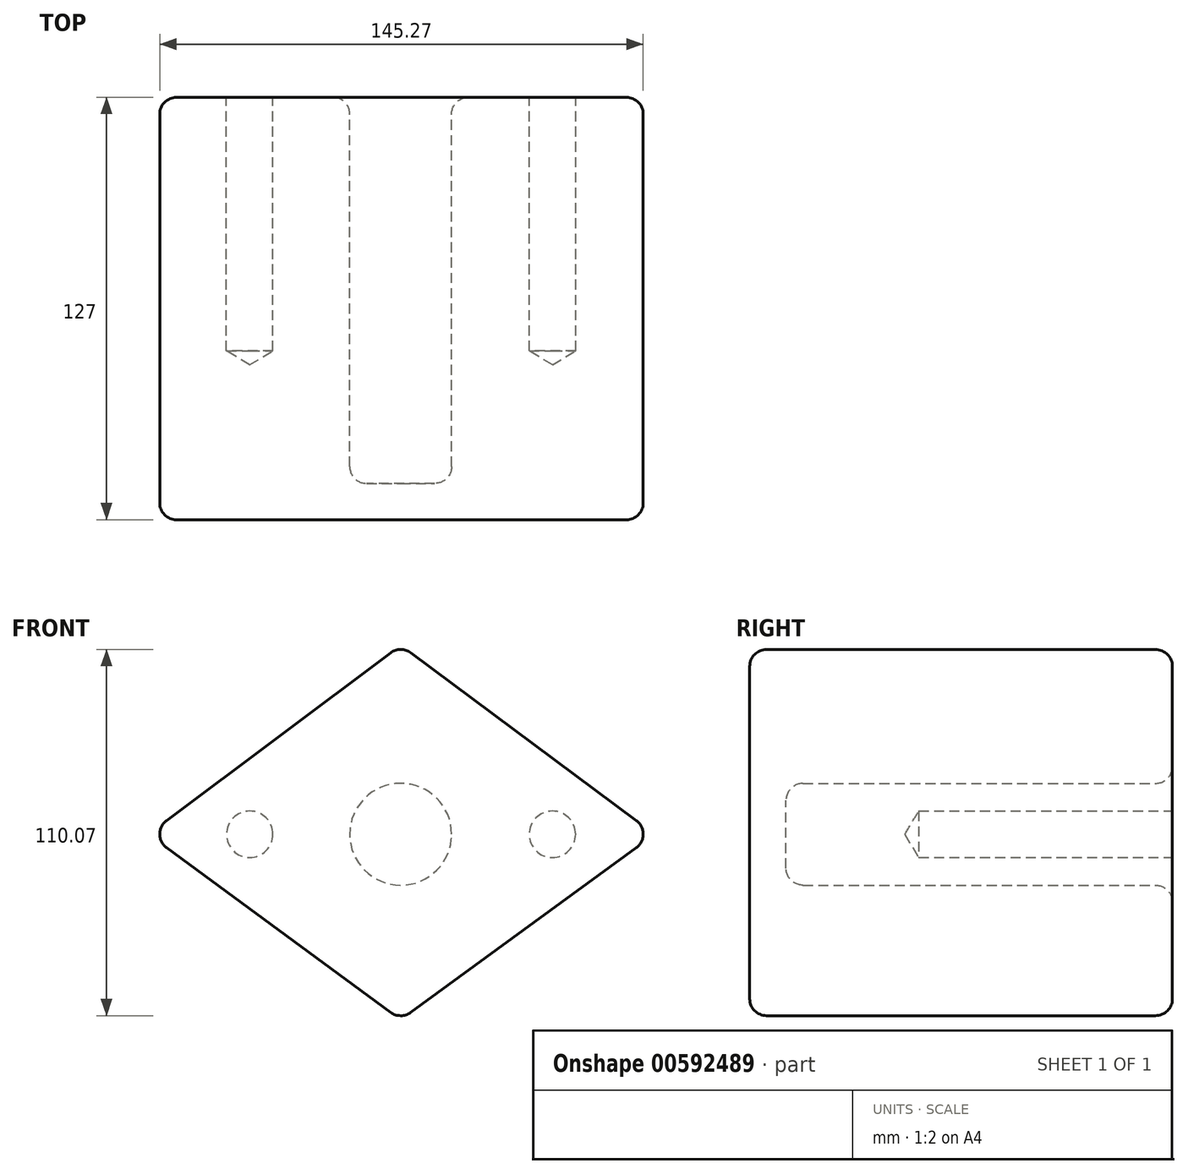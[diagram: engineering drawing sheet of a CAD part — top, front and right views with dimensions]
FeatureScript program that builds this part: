
annotation { "Feature Type Name" : "Feature", "Feature Type Description" : "" }
export const myFeature = defineFeature(function(context is Context, id is Id, definition is map)
    precondition{}
    {
        {
            var Q0;
            Q0=qCreatedBy(makeId("Front.planeOp"),FACE);
            var sketch = newSketch(context, id + "F0", { "sketchPlane" : qUnion([Q0])});
            skLineSegment(sketch, "E0", {"start": v(0, 0) * mm, "end": v(0, 56.8) * mm});
            skLineSegment(sketch, "E1", {"start": v(0, 56.8) * mm, "end": v(76.37, 0) * mm});
            skLineSegment(sketch, "E2", {"start": v(0, 0) * mm, "end": v(76.37, 0) * mm});
            skLineSegment(sketch, "E3", {"start": v(0, 0) * mm, "end": v(0, -55.74) * mm});
            skLineSegment(sketch, "E4", {"start": v(76.37, 0) * mm, "end": v(0, -55.74) * mm});
            skLineSegment(sketch, "E5", {"start": v(0, 0) * mm, "end": v(-75.83, 0) * mm});
            skLineSegment(sketch, "E6", {"start": v(0, -55.74) * mm, "end": v(-75.83, 0) * mm});
            skLineSegment(sketch, "E7", {"start": v(-75.83, 0) * mm, "end": v(0, 56.8) * mm});
            skCircle(sketch, "E8", {"center": v(0, 0) * mm, "radius": 7.17 * mm});
            skSolve(sketch);
        }
        {
            var Q0;
            {var subQ0=sQuery(id+"F0.wireOp",EDGE,"E7");Q0=makeQuery(id+"F0.imprint","IMPRINT",FACE,{"disambiguationData":[TD([[makeQuery(id+"F0.imprint","IMPRINT",EDGE,{"derivedFrom":subQ0}),-1.0]])]});}
            var Q1;
            {var subQ0=sQuery(id+"F0.wireOp",EDGE,"E1");Q1=makeQuery(id+"F0.imprint","IMPRINT",FACE,{"disambiguationData":[TD([[makeQuery(id+"F0.imprint","IMPRINT",EDGE,{"derivedFrom":subQ0}),-1.0]])]});}
            var Q2;
            {var subQ0=sQuery(id+"F0.wireOp",EDGE,"E4");Q2=makeQuery(id+"F0.imprint","IMPRINT",FACE,{"disambiguationData":[TD([[makeQuery(id+"F0.imprint","IMPRINT",EDGE,{"derivedFrom":subQ0}),-1.0]])]});}
            var Q3;
            {var subQ0=sQuery(id+"F0.wireOp",EDGE,"E6");Q3=makeQuery(id+"F0.imprint","IMPRINT",FACE,{"disambiguationData":[TD([[makeQuery(id+"F0.imprint","IMPRINT",EDGE,{"derivedFrom":subQ0}),-1.0]])]});}
            var Q4;
            {var subQ1=sQuery(id+"F0.wireOp",EDGE,"E2");var subQ3=sQuery(id+"F0.wireOp",EDGE,"E8");var subQ4=makeQuery(id+"F0.imprint","INTERSECT",VERTEX,{"derivedFrom":[subQ1,subQ3]});Q4=makeQuery(id+"F0.imprint","IMPRINT",FACE,{"disambiguationData":[TD([[makeQuery(id+"F0.imprint","IMPRINT",EDGE,{"disambiguationData":[TD([[subQ4,1.0]])],"derivedFrom":subQ3}),1.0]])]});}
            var Q5;
            {var subQ1=sQuery(id+"F0.wireOp",EDGE,"E0");var subQ3=sQuery(id+"F0.wireOp",EDGE,"E8");var subQ4=makeQuery(id+"F0.imprint","INTERSECT",VERTEX,{"derivedFrom":[subQ1,subQ3]});Q5=makeQuery(id+"F0.imprint","IMPRINT",FACE,{"disambiguationData":[TD([[makeQuery(id+"F0.imprint","IMPRINT",EDGE,{"disambiguationData":[TD([[subQ4,-1.0]])],"derivedFrom":subQ3}),1.0]])]});}
            var Q6;
            {var subQ1=sQuery(id+"F0.wireOp",EDGE,"E0");var subQ3=sQuery(id+"F0.wireOp",EDGE,"E8");var subQ4=makeQuery(id+"F0.imprint","INTERSECT",VERTEX,{"derivedFrom":[subQ1,subQ3]});Q6=makeQuery(id+"F0.imprint","IMPRINT",FACE,{"disambiguationData":[TD([[makeQuery(id+"F0.imprint","IMPRINT",EDGE,{"disambiguationData":[TD([[subQ4,1.0]])],"derivedFrom":subQ3}),1.0]])]});}
            var Q7;
            {var subQ1=sQuery(id+"F0.wireOp",EDGE,"E3");var subQ3=sQuery(id+"F0.wireOp",EDGE,"E8");var subQ4=makeQuery(id+"F0.imprint","INTERSECT",VERTEX,{"derivedFrom":[subQ1,subQ3]});Q7=makeQuery(id+"F0.imprint","IMPRINT",FACE,{"disambiguationData":[TD([[makeQuery(id+"F0.imprint","IMPRINT",EDGE,{"disambiguationData":[TD([[subQ4,1.0]])],"derivedFrom":subQ3}),1.0]])]});}
            extrude(context, id + "F1", {"entities" : qUnion([Q0, Q1, Q2, Q3, Q4, Q5, Q6, Q7]), "depth" : 25.4 * mm, "offsetDistance" : 25.4 * mm});
        }
        {
            var Q0;
            Q0=qCreatedBy(makeId("Front.planeOp"),FACE);
            var sketch = newSketch(context, id + "F2", { "sketchPlane" : qUnion([Q0])});
            skPoint(sketch, "E9", {"position": v(0, 0) * mm});
            skCircle(sketch, "E10", {"center": v(0, 0) * mm, "radius": 15.3 * mm});
            skSolve(sketch);
        }
        {
            var Q0;
            Q0=makeQuery(id+"F2.imprint","IMPRINT",FACE,{"disambiguationData":[TD([[makeQuery(id+"F2.imprint","IMPRINT",EDGE,{"derivedFrom":sQuery(id+"F2.wireOp",EDGE,"E10")}),1.0]])]});
            extrude(context, id + "F3", {"entities" : qUnion([Q0]), "operationType" : NewBodyOperationType.REMOVE, "depth" : 14.48 * mm, "offsetDistance" : 25.4 * mm});
        }
        {
            var Q0;
            Q0=makeQuery(id+"F1.opExtrude","CAP_FACE",FACE,{"disambiguationData":[OSD([sQuery(id+"F0.wireOp",EDGE,"E1"),sQuery(id+"F0.wireOp",EDGE,"E4"),sQuery(id+"F0.wireOp",EDGE,"E6"),sQuery(id+"F0.wireOp",EDGE,"E7")])],"isStart":true});
            extrude(context, id + "F4", {"entities" : qUnion([Q0]), "operationType" : NewBodyOperationType.ADD, "depth" : 101.6 * mm, "offsetDistance" : 25.4 * mm});
        }
        {
            var Q0;
            Q0=makeQuery(id+"F4.opExtrude","CAP_FACE",FACE,{"disambiguationData":[OSD([sQuery(id+"F0.wireOp",EDGE,"E1"),sQuery(id+"F0.wireOp",EDGE,"E4"),sQuery(id+"F0.wireOp",EDGE,"E6"),sQuery(id+"F0.wireOp",EDGE,"E7")])],"isStart":false});
            var sketch = newSketch(context, id + "F5", { "sketchPlane" : qUnion([Q0])});
            skCircle(sketch, "E11", {"center": v(-45.6, 0) * mm, "radius": 9.34 * mm});
            skCircle(sketch, "E12", {"center": v(47.08, 0) * mm, "radius": 9.04 * mm});
            skSolve(sketch);
        }
        {
            var Q0;
            Q0=sQuery(id+"F5.wireOp",VERTEX,"E11.center");
            var Q1;
            Q1=makeQuery(id+"F1.opExtrude","SWEPT_BODY",BODY,{"disambiguationData":[OSD([sQuery(id+"F0.wireOp",EDGE,"E1"),sQuery(id+"F0.wireOp",EDGE,"E4"),sQuery(id+"F0.wireOp",EDGE,"E6"),sQuery(id+"F0.wireOp",EDGE,"E7")])]});
            hole(context, id + "F6", {"style" : HoleStyle.C_BORE, "endStyle" : HoleEndStyle.BLIND, "holeDiameter" : 13.97 * mm, "cBoreDiameter" : 13.97 * mm, "cBoreDepth" : 6.35 * mm, "majorDiameter" : 6.35 * mm, "holeDepth" : 76.2 * mm, "isTappedThrough" : true, "tappedDepth" : 12.7 * mm, "tapClearance" : 3, "locations" : qUnion([Q0]), "scope" : qUnion([Q1])});
        }
        {
            var Q0;
            Q0=makeQuery(id+"F4.opExtrude","CAP_FACE",FACE,{"disambiguationData":[OSD([sQuery(id+"F0.wireOp",EDGE,"E1"),sQuery(id+"F0.wireOp",EDGE,"E4"),sQuery(id+"F0.wireOp",EDGE,"E6"),sQuery(id+"F0.wireOp",EDGE,"E7")])],"isStart":false});
            var sketch = newSketch(context, id + "F7", { "sketchPlane" : qUnion([Q0])});
            skCircle(sketch, "E13", {"center": v(45.35, 0) * mm, "radius": 9.24 * mm});
            skSolve(sketch);
        }
        {
            var Q0;
            Q0=sQuery(id+"F7.wireOp",VERTEX,"E13.center");
            var Q1;
            Q1=makeQuery(id+"F1.opExtrude","SWEPT_BODY",BODY,{"disambiguationData":[OSD([sQuery(id+"F0.wireOp",EDGE,"E1"),sQuery(id+"F0.wireOp",EDGE,"E4"),sQuery(id+"F0.wireOp",EDGE,"E6"),sQuery(id+"F0.wireOp",EDGE,"E7")])]});
            hole(context, id + "F8", {"style" : HoleStyle.C_BORE, "endStyle" : HoleEndStyle.BLIND, "holeDiameter" : 13.97 * mm, "cBoreDiameter" : 13.97 * mm, "cBoreDepth" : 6.35 * mm, "majorDiameter" : 6.35 * mm, "holeDepth" : 76.2 * mm, "isTappedThrough" : true, "tappedDepth" : 12.7 * mm, "tapClearance" : 3, "locations" : qUnion([Q0]), "scope" : qUnion([Q1])});
        }
        {
            var Q0;
            Q0=makeQuery(id+"F4.opExtrude","CAP_EDGE",EDGE,{"disambiguationData":[OSD([sQuery(id+"F0.wireOp",EDGE,"E1")])],"isStart":false});
            var Q1;
            Q1=makeQuery(id+"F4.opExtrude","CAP_EDGE",EDGE,{"disambiguationData":[OSD([sQuery(id+"F0.wireOp",EDGE,"E4")])],"isStart":false});
            var Q2;
            Q2=makeQuery(id+"F6.hole-0.boolean.opBoolean","COPY",FACE,{"derivedFrom":makeQuery(id+"F6.hole-0.opRevolve","SWEPT_FACE",FACE,{"disambiguationData":[OSD([sQuery(id+"F6.hole-0.sketch.wireOp",EDGE,"core_line_1")])]})});
            var Q3;
            Q3=makeQuery(id+"F3.boolean.opBoolean","COPY",FACE,{"derivedFrom":makeQuery(id+"F3.opExtrude","CAP_FACE",FACE,{"disambiguationData":[OSD([sQuery(id+"F2.wireOp",EDGE,"E10")])],"isStart":false})});
            var Q4;
            Q4=makeQuery(id+"F8.hole-0.boolean.opBoolean","COPY",FACE,{"derivedFrom":makeQuery(id+"F8.hole-0.opRevolve","SWEPT_FACE",FACE,{"disambiguationData":[OSD([sQuery(id+"F8.hole-0.sketch.wireOp",EDGE,"core_line_1")])]})});
            var Q5;
            Q5=makeQuery(id+"F4.opExtrude","CAP_EDGE",EDGE,{"disambiguationData":[OSD([sQuery(id+"F2.wireOp",EDGE,"E10")])],"isStart":false});
            var Q6;
            Q6=makeQuery(id+"F8.hole-0.boolean.opBoolean","COPY",EDGE,{"derivedFrom":makeQuery(id+"F8.hole-0.opRevolve","SWEPT_EDGE",EDGE,{"disambiguationData":[OSD([sQuery(id+"F8.hole-0.sketch.wireOp",EDGE,"core_line_2"),sQuery(id+"F8.hole-0.sketch.wireOp",EDGE,"core_line_3")])]})});
            var Q7;
            Q7=makeQuery(id+"F6.hole-0.boolean.opBoolean","COPY",EDGE,{"derivedFrom":makeQuery(id+"F6.hole-0.opRevolve","SWEPT_EDGE",EDGE,{"disambiguationData":[OSD([sQuery(id+"F6.hole-0.sketch.wireOp",EDGE,"core_line_2"),sQuery(id+"F6.hole-0.sketch.wireOp",EDGE,"core_line_3")])]})});
            var Q8;
            {var subQ0=sQuery(id+"F0.wireOp",EDGE,"E6");Q8=makeQuery(id+"F4.boolean.opBoolean","MERGE",FACE,{"derivedFrom":[makeQuery(id+"F1.opExtrude","SWEPT_FACE",FACE,{"disambiguationData":[OSD([subQ0])]}),makeQuery(id+"F4.opExtrude","SWEPT_FACE",FACE,{"disambiguationData":[OSD([subQ0])]})]});}
            var Q9;
            {var subQ0=sQuery(id+"F0.wireOp",EDGE,"E7");Q9=makeQuery(id+"F4.boolean.opBoolean","MERGE",FACE,{"derivedFrom":[makeQuery(id+"F1.opExtrude","SWEPT_FACE",FACE,{"disambiguationData":[OSD([subQ0])]}),makeQuery(id+"F4.opExtrude","SWEPT_FACE",FACE,{"disambiguationData":[OSD([subQ0])]})]});}
            var Q10;
            Q10=makeQuery(id+"F1.opExtrude","CAP_FACE",FACE,{"disambiguationData":[OSD([sQuery(id+"F0.wireOp",EDGE,"E1"),sQuery(id+"F0.wireOp",EDGE,"E4"),sQuery(id+"F0.wireOp",EDGE,"E6"),sQuery(id+"F0.wireOp",EDGE,"E7")])],"isStart":false});
            var Q11;
            {var subQ0=sQuery(id+"F0.wireOp",EDGE,"E4");Q11=makeQuery(id+"F4.boolean.opBoolean","MERGE",FACE,{"derivedFrom":[makeQuery(id+"F1.opExtrude","SWEPT_FACE",FACE,{"disambiguationData":[OSD([subQ0])]}),makeQuery(id+"F4.opExtrude","SWEPT_FACE",FACE,{"disambiguationData":[OSD([subQ0])]})]});}
            fillet(context, id + "F9", {"entities" : qUnion([Q0, Q1, Q2, Q3, Q4, Q5, Q6, Q7, Q8, Q9, Q10, Q11]), "radius" : 5.08 * mm, "tangentPropagation" : true, "allowEdgeOverflow" : false});
        }
    });
